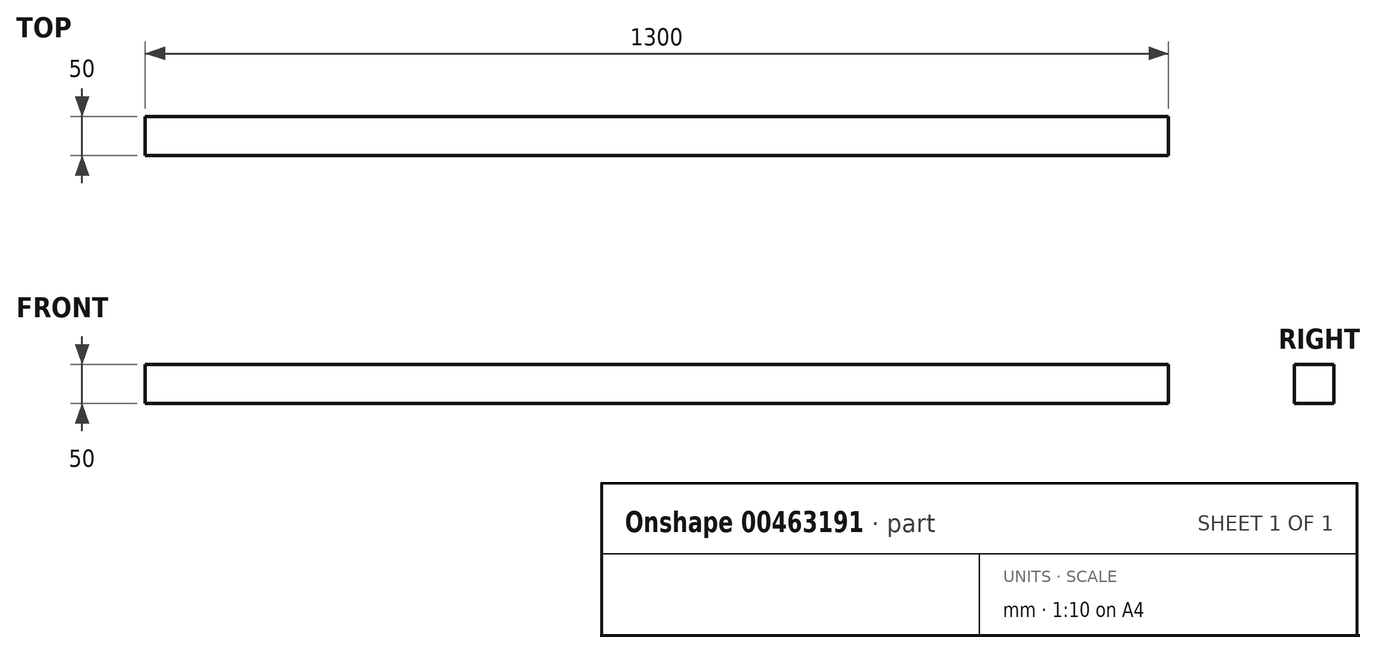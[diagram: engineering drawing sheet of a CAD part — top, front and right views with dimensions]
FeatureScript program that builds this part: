
annotation { "Feature Type Name" : "Feature", "Feature Type Description" : "" }
export const myFeature = defineFeature(function(context is Context, id is Id, definition is map)
    precondition{}
    {
        {
            var Q0;
            Q0=qCreatedBy(makeId("Top.planeOp"),FACE);
            var sketch = newSketch(context, id + "F0", { "sketchPlane" : qUnion([Q0])});
            skLineSegment(sketch, "E0.bottom", {"start": v(0, 0) * mm, "end": v(1300, 0) * mm});
            skLineSegment(sketch, "E0.top", {"start": v(0, -50) * mm, "end": v(1300, -50) * mm});
            skLineSegment(sketch, "E0.left", {"start": v(0, 0) * mm, "end": v(0, -50) * mm});
            skLineSegment(sketch, "E0.right", {"start": v(1300, 0) * mm, "end": v(1300, -50) * mm});
            skSolve(sketch);
        }
        {
            var Q0;
            Q0=makeQuery(id+"F0.imprint","IMPRINT",FACE,{"disambiguationData":[TD([[makeQuery(id+"F0.imprint","IMPRINT",EDGE,{"derivedFrom":sQuery(id+"F0.wireOp",EDGE,"E0.bottom")}),-1.0]])]});
            extrude(context, id + "F1", {"entities" : qUnion([Q0]), "depth" : 50 * mm});
        }
    });
